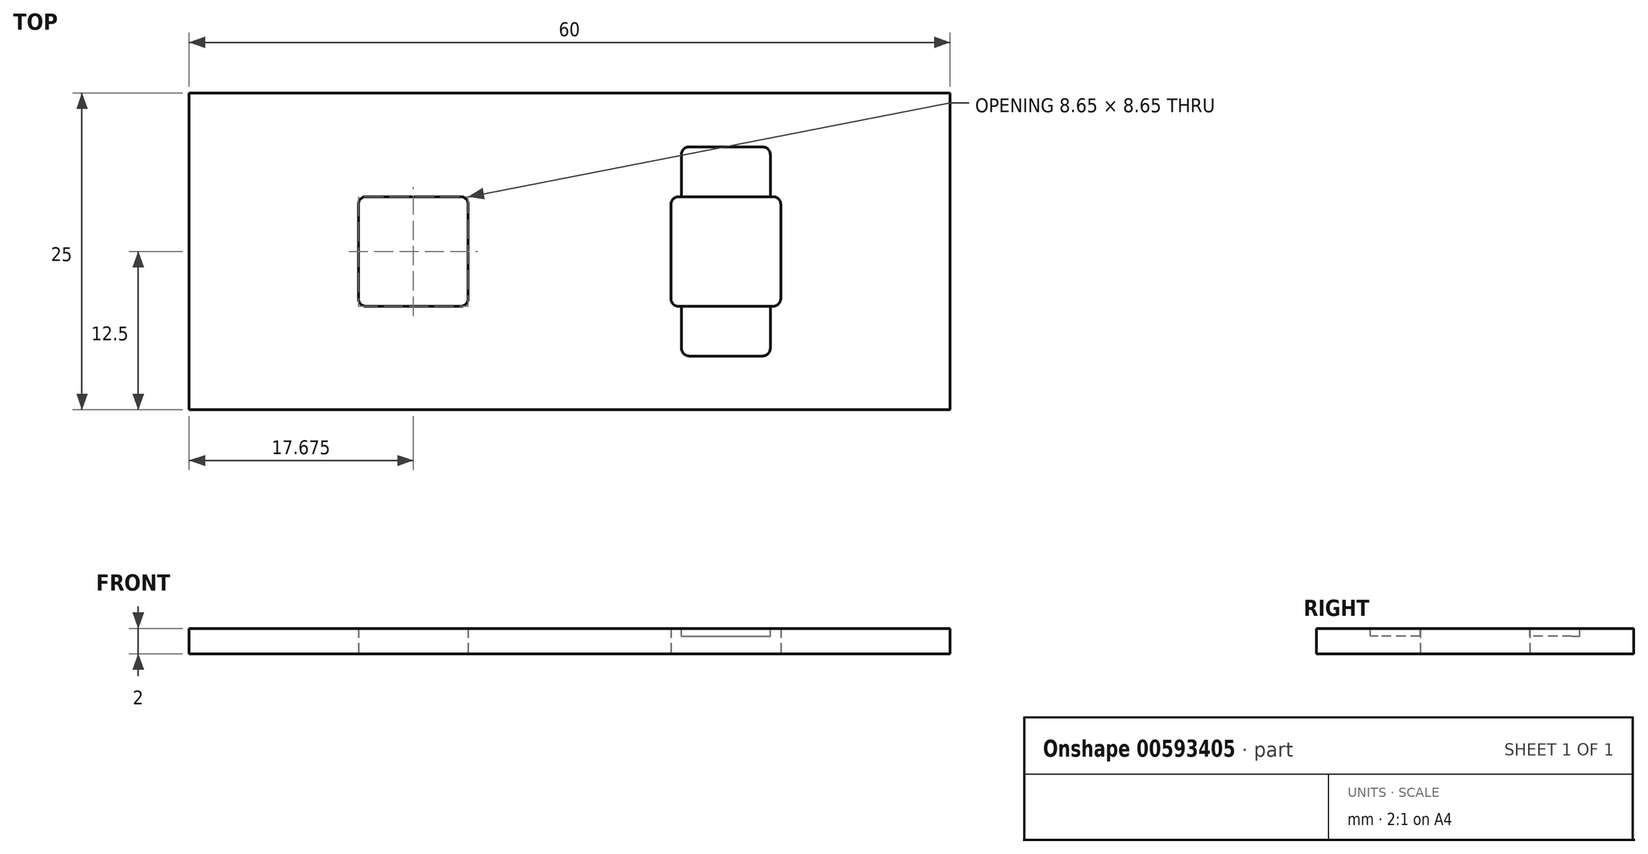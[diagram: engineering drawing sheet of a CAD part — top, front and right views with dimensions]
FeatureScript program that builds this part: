
annotation { "Feature Type Name" : "Feature", "Feature Type Description" : "" }
export const myFeature = defineFeature(function(context is Context, id is Id, definition is map)
    precondition{}
    {
        {
            var Q0;
            Q0=qCreatedBy(makeId("Top.planeOp"),FACE);
            var sketch = newSketch(context, id + "F0", { "sketchPlane" : qUnion([Q0])});
            skLineSegment(sketch, "E0.bottom", {"start": v(-30, 12.5) * mm, "end": v(30, 12.5) * mm});
            skLineSegment(sketch, "E0.top", {"start": v(-30, -12.5) * mm, "end": v(30, -12.5) * mm});
            skLineSegment(sketch, "E0.left", {"start": v(-30, 12.5) * mm, "end": v(-30, -12.5) * mm});
            skLineSegment(sketch, "E0.right", {"start": v(30, 12.5) * mm, "end": v(30, -12.5) * mm});
            skLineSegment(sketch, "E1.bottom", {"start": v(-16.05, 4.33) * mm, "end": v(-8.6, 4.33) * mm});
            skLineSegment(sketch, "E1.top", {"start": v(-16.05, -4.33) * mm, "end": v(-8.6, -4.33) * mm});
            skLineSegment(sketch, "E1.left", {"start": v(-16.65, 3.73) * mm, "end": v(-16.65, -3.73) * mm});
            skLineSegment(sketch, "E1.right", {"start": v(-8, 3.73) * mm, "end": v(-8, -3.73) * mm});
            skLineSegment(sketch, "E2.bottom", {"start": v(8.6, 4.33) * mm, "end": v(16.05, 4.33) * mm});
            skLineSegment(sketch, "E2.top", {"start": v(8.6, -4.32) * mm, "end": v(16.05, -4.32) * mm});
            skLineSegment(sketch, "E2.left", {"start": v(8, 3.73) * mm, "end": v(8, -3.72) * mm});
            skLineSegment(sketch, "E2.right", {"start": v(16.65, 3.73) * mm, "end": v(16.65, -3.72) * mm});
            skPoint(sketch, "E3.visualSharp", {"position": v(-16.65, 4.33) * mm});
            skArc(sketch, "E3.filletArc", {"start": v(-16.05, 4.33) * mm, "mid": v(-16.47, 4.15) * mm, "end": v(-16.65, 3.73) * mm});
            skPoint(sketch, "E4.visualSharp", {"position": v(-16.65, -4.33) * mm});
            skArc(sketch, "E4.filletArc", {"start": v(-16.65, -3.73) * mm, "mid": v(-16.47, -4.15) * mm, "end": v(-16.05, -4.33) * mm});
            skPoint(sketch, "E5.visualSharp", {"position": v(-8, -4.33) * mm});
            skArc(sketch, "E5.filletArc", {"start": v(-8.6, -4.32) * mm, "mid": v(-8.18, -4.15) * mm, "end": v(-8, -3.73) * mm});
            skPoint(sketch, "E6.visualSharp", {"position": v(-8, 4.33) * mm});
            skArc(sketch, "E6.filletArc", {"start": v(-8, 3.73) * mm, "mid": v(-8.18, 4.15) * mm, "end": v(-8.6, 4.33) * mm});
            skPoint(sketch, "E7.visualSharp", {"position": v(8, 4.33) * mm});
            skArc(sketch, "E7.filletArc", {"start": v(8.6, 4.33) * mm, "mid": v(8.18, 4.15) * mm, "end": v(8, 3.73) * mm});
            skPoint(sketch, "E8.visualSharp", {"position": v(8, -4.32) * mm});
            skArc(sketch, "E8.filletArc", {"start": v(8, -3.72) * mm, "mid": v(8.18, -4.15) * mm, "end": v(8.6, -4.32) * mm});
            skPoint(sketch, "E9.visualSharp", {"position": v(16.65, -4.32) * mm});
            skArc(sketch, "E9.filletArc", {"start": v(16.05, -4.32) * mm, "mid": v(16.47, -4.15) * mm, "end": v(16.65, -3.72) * mm});
            skPoint(sketch, "E10.visualSharp", {"position": v(16.65, 4.33) * mm});
            skArc(sketch, "E10.filletArc", {"start": v(16.65, 3.73) * mm, "mid": v(16.47, 4.15) * mm, "end": v(16.05, 4.33) * mm});
            skSolve(sketch);
        }
        {
            var Q0;
            Q0=makeQuery(id+"F0.imprint","IMPRINT",FACE,{"disambiguationData":[TD([[makeQuery(id+"F0.imprint","IMPRINT",EDGE,{"derivedFrom":sQuery(id+"F0.wireOp",EDGE,"E0.bottom")}),-1.0]])]});
            extrude(context, id + "F1", {"entities" : qUnion([Q0]), "depth" : 2 * mm, "offsetDistance" : 25 * mm});
        }
        {
            var Q0;
            Q0=makeQuery(id+"F1.opExtrude","CAP_FACE",FACE,{"disambiguationData":[OSD([sQuery(id+"F0.wireOp",EDGE,"E0.bottom"),sQuery(id+"F0.wireOp",EDGE,"E0.top"),sQuery(id+"F0.wireOp",EDGE,"E0.left"),sQuery(id+"F0.wireOp",EDGE,"E0.right"),sQuery(id+"F0.wireOp",EDGE,"E1.bottom"),sQuery(id+"F0.wireOp",EDGE,"E1.top"),sQuery(id+"F0.wireOp",EDGE,"E1.left"),sQuery(id+"F0.wireOp",EDGE,"E1.right"),sQuery(id+"F0.wireOp",EDGE,"E2.bottom"),sQuery(id+"F0.wireOp",EDGE,"E2.top"),sQuery(id+"F0.wireOp",EDGE,"E2.left"),sQuery(id+"F0.wireOp",EDGE,"E2.right"),sQuery(id+"F0.wireOp",EDGE,"E3.filletArc"),sQuery(id+"F0.wireOp",EDGE,"E4.filletArc"),sQuery(id+"F0.wireOp",EDGE,"E5.filletArc"),sQuery(id+"F0.wireOp",EDGE,"E6.filletArc"),sQuery(id+"F0.wireOp",EDGE,"E7.filletArc"),sQuery(id+"F0.wireOp",EDGE,"E8.filletArc"),sQuery(id+"F0.wireOp",EDGE,"E9.filletArc"),sQuery(id+"F0.wireOp",EDGE,"E10.filletArc")])],"isStart":false});
            var sketch = newSketch(context, id + "F2", { "sketchPlane" : qUnion([Q0])});
            skLineSegment(sketch, "E11.bottom", {"start": v(9.43, 8.25) * mm, "end": v(15.22, 8.25) * mm});
            skLineSegment(sketch, "E11.top", {"start": v(9.42, -8.25) * mm, "end": v(15.22, -8.25) * mm});
            skLineSegment(sketch, "E11.left", {"start": v(8.83, 7.65) * mm, "end": v(8.82, -7.65) * mm});
            skLineSegment(sketch, "E11.right", {"start": v(15.82, 7.65) * mm, "end": v(15.82, -7.65) * mm});
            skLineSegment(sketch, "E12", {"start": v(8.82, 8.25) * mm, "end": v(15.82, -8.25) * mm, "construction": true});
            skLineSegment(sketch, "E13", {"start": v(8, 3.73) * mm, "end": v(16.65, -3.72) * mm, "construction": true});
            skPoint(sketch, "E14", {"position": v(12.32, 0) * mm});
            skPoint(sketch, "E15.visualSharp", {"position": v(15.82, 8.25) * mm});
            skArc(sketch, "E15.filletArc", {"start": v(15.82, 7.65) * mm, "mid": v(15.65, 8.07) * mm, "end": v(15.22, 8.25) * mm});
            skPoint(sketch, "E16.visualSharp", {"position": v(8.83, 8.25) * mm});
            skArc(sketch, "E16.filletArc", {"start": v(9.43, 8.25) * mm, "mid": v(9, 8.07) * mm, "end": v(8.83, 7.65) * mm});
            skPoint(sketch, "E17.visualSharp", {"position": v(15.82, -8.25) * mm});
            skArc(sketch, "E17.filletArc", {"start": v(15.22, -8.25) * mm, "mid": v(15.65, -8.07) * mm, "end": v(15.82, -7.65) * mm});
            skPoint(sketch, "E18.visualSharp", {"position": v(8.82, -8.25) * mm});
            skArc(sketch, "E18.filletArc", {"start": v(8.82, -7.65) * mm, "mid": v(9, -8.07) * mm, "end": v(9.42, -8.25) * mm});
            skSolve(sketch);
        }
        {
            var Q0;
            Q0=makeQuery(id+"F2.imprint","IMPRINT",FACE,{"disambiguationData":[TD([[makeQuery(id+"F2.imprint","IMPRINT",EDGE,{"derivedFrom":sQuery(id+"F2.wireOp",EDGE,"E11.bottom")}),-1.0]])]});
            var Q1;
            Q1=makeQuery(id+"F2.imprint","IMPRINT",FACE,{"disambiguationData":[TD([[makeQuery(id+"F2.imprint","IMPRINT",EDGE,{"derivedFrom":sQuery(id+"F2.wireOp",EDGE,"E11.top")}),1.0]])]});
            extrude(context, id + "F3", {"entities" : qUnion([Q0, Q1]), "operationType" : NewBodyOperationType.REMOVE, "oppositeDirection" : true, "depth" : 0.6 * mm, "offsetDistance" : 25 * mm});
        }
    });
